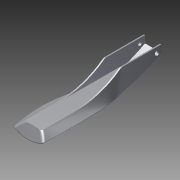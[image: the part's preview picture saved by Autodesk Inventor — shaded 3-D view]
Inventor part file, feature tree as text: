
AUTODESK INVENTOR PART (.ipt)
format: ipt  version: 2011 (Build 150239000, 239)  size: 672,768 bytes
history: native  units: mm (DEFAULTED — no unit token found)
features: other x18, sketch x12, extrude x8, fillet x5, surface_op x4, loft x3, plane x2, delete_face x1, split x1, sweep x1, revolve x1
ambient origin geometry x8: Origin, YZ Plane, XZ Plane, XY Plane, X Axis, Y Axis, Z Axis, Center Point
bodies: Solid1 (feature_tree)
feature tree (56):
  extrude  "Extrusion1"  Depth=19.05mm
  surface_op  "Replace Face1"
  extrude  "Extrusion2"  Depth=177.8mm
  extrude  "Extrusion3"  Depth=50.8mm
  fillet  "Fillet2"  [1 undecoded]
  sketch  "3D Sketch1"
  sketch  "3D Sketch2"
  delete_face  "Delete Face1"
  surface_op  "Stitch Surface5"
  plane  "Work Plane4"
  extrude  "Extrusion5"  Depth=158.75mm
  split  "Split1"
  fillet  "Fillet4"  Radius=31.75mm
  other  "Split Line"
  other  "Work Point1"
  other  "Hinge"
  extrude  "Extrusion6"  Depth=50.8mm
  fillet  "Fillet14"  Radius=107.95mm
  fillet  "Fillet6"  Radius=101.6mm
  plane  "Work Plane3"
  extrude  "Extrusion9"  Depth=50.8mm TaperAngle=0.0deg
  fillet  "Fillet12"  Radius=50.8mm
  sketch  "Sketch2"  dims[d1=158.75mm d2=19.05mm]
  sketch  "Sketch3"  dims[d3=1.524mm d5=177.8mm]
  other  "Srf1"
  sketch  "Sketch4"  dims[d6=9.525mm d7=50.8mm d8=0.0mm]
  sketch  "Sketch5"  dims[d9=47.625mm d10=158.75mm d11=31.75mm d12=0.0mm]
  sketch  "Sketch6"  dims[d13=12.7mm d18=50.8mm d19=107.95mm d20=101.6mm d21=0.0mm]
  other  "Srf2"
  sketch  "Sketch7"  dims[d23=22.225mm d25=50.8mm d26=0.0mm d27=50.8mm]
  sketch  "Sketch9"  dims[d28=12.7mm d29=114.3mm]
  sketch  "Sketch10"  dims[d30=22.225mm d31=19.05mm]
  other  "Srf8"
  sketch  "Sketch14"  dims[d32=50.8mm d33=114.3mm]
  sketch  "Sketch17"  dims[d34=19.05mm d35=22.225mm d36=12.7mm d37=50.8mm d38=0.0mm d82=6.35mm d100=25.4mm d101=0.0mm d106=254.0mm d107=6.35mm d108=73.025mm d109=152.4mm d110=90.0deg d111=3.175mm d115=104.775mm d117=38.1mm d118=4.7752mm d119=25.4mm d120=0.0mm d122=0.762mm d123=31.75mm d141=38.1mm d144=174.625mm d145=19.05mm d146=0.0mm d147=12.7mm d149=50.8mm d150=0.0mm d151=6.35mm d152=0.0mm d153=90.0deg d154=0.0mm d155=90.0deg d156=0.0mm d157=90.0deg d158=0.0mm d159=90.0deg d160=0.0mm d161=90.0deg d162=0.0mm d163=90.0deg d164=6.35mm d165=6.35mm d166=82.55mm d167=3.81mm d168=0.254mm]
  other  "Srf9"
  other  "Edges21"
  other  "Srf3"
  other  "Edges22"
  other  "Srf4"
  other  "Edges23"
  other  "Edges24"
  other  "Srf5"
  other  "Srf6"
  other  "Srf7"
  sweep  "SweepSrf1"
  extrude  "ExtrusionSrf1"  Depth=19.05mm
  loft  "LoftSrf11"
  loft  "LoftSrf12"
  loft  "LoftSrf13"
  surface_op  "Boundary Patch1"
  surface_op  "Boundary Patch2"
  revolve  "RevolutionSrf1"  [1 undecoded]
  extrude  "ExtrusionSrf2"  Depth=6.35mm
  other  "3D Intersection1"
  other  "3D Intersection2"
note: 2 required parameter values undecoded (feature->parameter linkage not recoverable at this tier; creation-order binding heuristic only, values carry confidence <= 0.55)